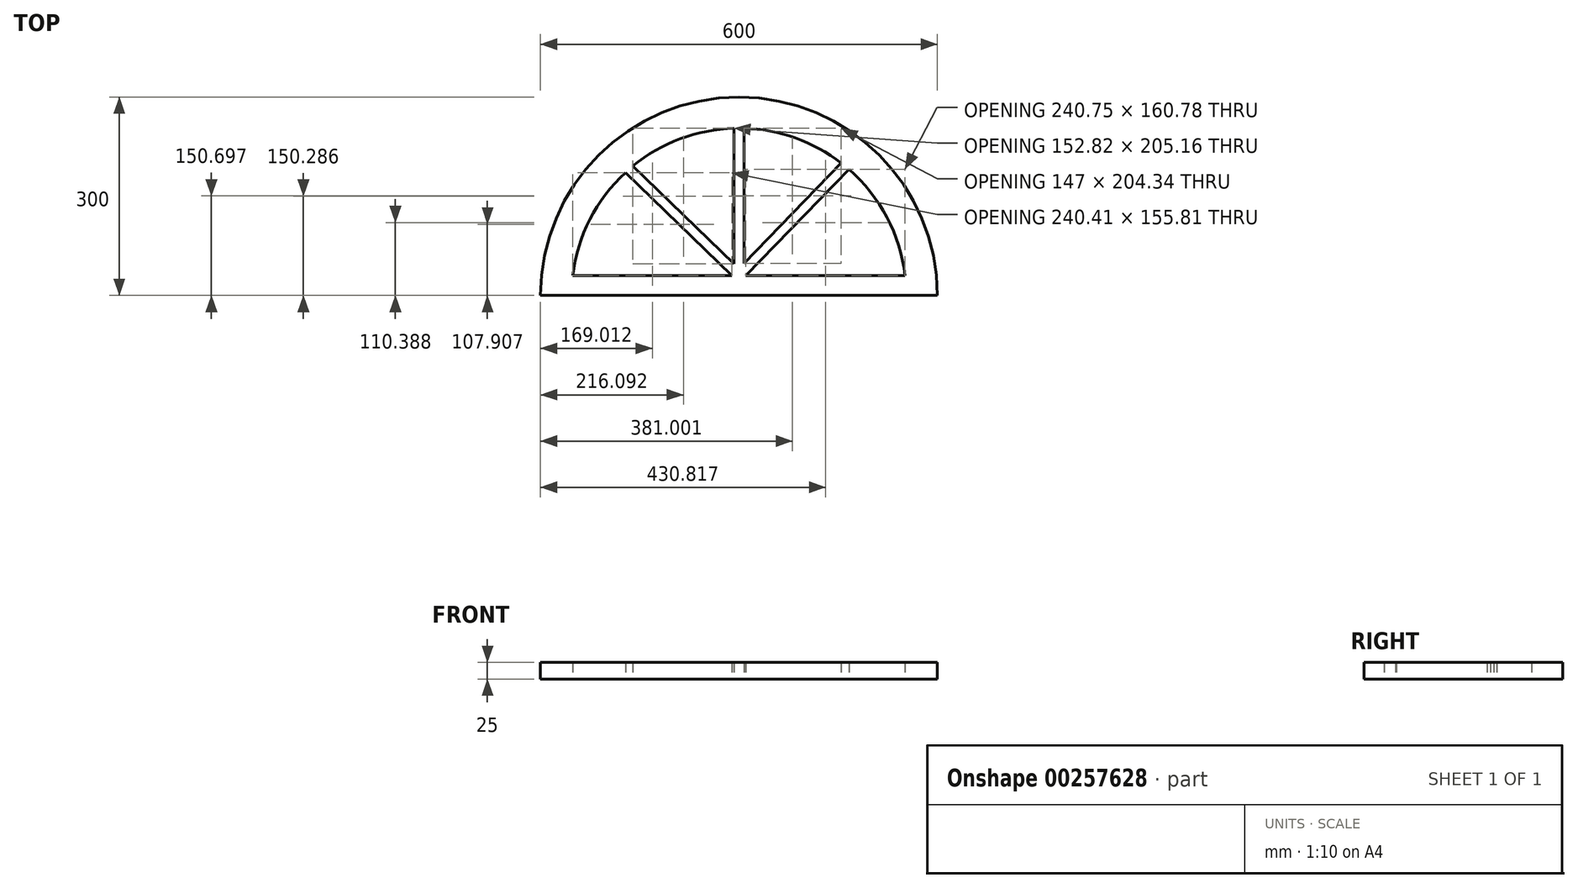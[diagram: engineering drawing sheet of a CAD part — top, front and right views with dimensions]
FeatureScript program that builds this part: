
annotation { "Feature Type Name" : "Feature", "Feature Type Description" : "" }
export const myFeature = defineFeature(function(context is Context, id is Id, definition is map)
    precondition{}
    {
        {
            var Q0;
            Q0=qCreatedBy(makeId("Top.planeOp"),FACE);
            var sketch = newSketch(context, id + "F0", { "sketchPlane" : qUnion([Q0])});
            skArc(sketch, "E0", {"start": v(300, 0) * mm, "mid": v(0, 300) * mm, "end": v(-300, 0) * mm});
            skLineSegment(sketch, "E1", {"start": v(0, 0) * mm, "end": v(300, 0) * mm});
            skArc(sketch, "E2", {"start": v(251.2, 30) * mm, "mid": v(223.62, 118.3) * mm, "end": v(166.14, 190.78) * mm});
            skLineSegment(sketch, "E3", {"start": v(-251.2, 30) * mm, "end": v(251.2, 30) * mm});
            skLineSegment(sketch, "E4", {"start": v(-300, 0) * mm, "end": v(300, 0) * mm});
            skPoint(sketch, "E5.end.orphan", {"position": v(-225.87, 30) * mm});
            skLineSegment(sketch, "E6", {"start": v(-124.94, 140.56) * mm, "end": v(-10.78, 30) * mm});
            skLineSegment(sketch, "E7", {"start": v(-160.32, 195.7) * mm, "end": v(-7.5, 47.7) * mm});
            skLineSegment(sketch, "E8", {"start": v(-124.94, 140.56) * mm, "end": v(-171.67, 185.81) * mm});
            skArc(sketch, "E9.trimOffspring", {"start": v(-171.67, 185.81) * mm, "mid": v(-225.33, 115) * mm, "end": v(-251.2, 30) * mm});
            skLineSegment(sketch, "E10", {"start": v(-7.5, 187.73) * mm, "end": v(-7.5, 252.87) * mm});
            skLineSegment(sketch, "E11", {"start": v(-7.5, 252.87) * mm, "end": v(-7.5, 47.7) * mm});
            skLineSegment(sketch, "E12", {"start": v(7.5, 187.73) * mm, "end": v(7.5, 252.87) * mm});
            skLineSegment(sketch, "E13", {"start": v(7.5, 252.87) * mm, "end": v(7.5, 48.53) * mm});
            skLineSegment(sketch, "E14", {"start": v(115.54, 160.09) * mm, "end": v(154.5, 200.32) * mm});
            skLineSegment(sketch, "E15", {"start": v(154.5, 200.32) * mm, "end": v(7.5, 48.53) * mm});
            skLineSegment(sketch, "E16", {"start": v(126.32, 149.65) * mm, "end": v(166.14, 190.78) * mm});
            skLineSegment(sketch, "E17", {"start": v(166.14, 190.78) * mm, "end": v(10.44, 30) * mm});
            skPoint(sketch, "E18.start.orphan", {"position": v(0, 30) * mm});
            skArc(sketch, "E19.trimOffspring", {"start": v(-7.5, 252.87) * mm, "mid": v(-88.64, 236.94) * mm, "end": v(-160.32, 195.7) * mm});
            skArc(sketch, "E20.trimOffspring", {"start": v(154.5, 200.32) * mm, "mid": v(85.16, 238.22) * mm, "end": v(7.5, 252.87) * mm});
            skSolve(sketch);
        }
        {
            var Q0;
            Q0 = qSketchRegion(id + "F0", true);
            extrude(context, id + "F1", {"entities" : qUnion([Q0]), "depth" : 25 * mm});
        }
    });
